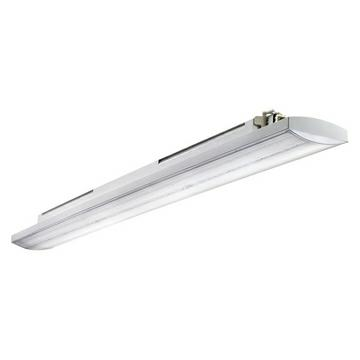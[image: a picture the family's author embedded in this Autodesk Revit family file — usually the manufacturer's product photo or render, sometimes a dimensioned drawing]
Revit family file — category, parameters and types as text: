
# Revit family: Lighting-Industriale-GEWISS-SMART[3]PLUS-PLAFONIERA-LED_TRANSPARENTE_FASCIOMEDIO_1600mm
name_source: partatom
category: Apparecchi per illuminazione
units: mm (PartAtom-declared; Revit-internal decimal feet)

## family parameters
Condiviso = No
Host = Superficie
Punto di calcolo locali = No
Quota connettore circolare = Usa diametro
Sorgente d'illuminazione = Sì
Taglio con vuoti quando caricato = No
Tipo di parte = Normale

## types (1)
- Lighting-Industriale-GEWISS-SMART[3]PLUS-PLAFONIERA-LED_TRANSPARENTE_FASCIOMEDIO_1600mm
    Angolo inclinazione = -90.00°
    Applicazione = Interno
    Carico apparente = 67 VA
    Catalogo = LIGHTING
    Catalogo Serie = SMART[3] PLUS
    Classe di efficienza LED integrati = A ÷ A++
    Classe isolamento = II
    Codice Electrocod = 2434
    Commenti sul wattaggio = 67W
    Descrizione = SMART3 PLUS 1600 T.W.DALI HE CONC 9 57
    Emetti da lunghezza linea = 1200 mm
    File diagramma fotometrico = GWS3323AC957.IES
    Filtro dei colori = 16777215
    Ganci = Alluminio
    Garanzia = 5 anni
    Glow Wire Test = 850°C
    Grado di protezione = IP66/IP69
    IDF = b404d7be-e00a-44e9-bc86-c84b1d72c067
    IDT = fe96ae85-68db-4e0d-8c9b-145f0d7eb605
    Immagine tipo = GWS3280TS.jpg
    Lampada = LED
    Lampada: = LED
    Lumen output (lm) = 5600
    Lunghezza = 1600 mm
    Lunghezza Lampada = 1600 mm  [stored 5.24934 ft]
    Modello = GWS3323AC957
    Numero poli = 2
    Potenza di sistema = 50 W
    Produttore = GEWISS S.p.A.
    Prospetto di default = 1219 mm
    Resistenza agli urti = IK08
    SEO = Plafoniera
    Scheda Tecnica = https://www.gewiss.com
    Schermo = Trasparente
    Schermo. = Led Acceso
    Stampa 1_100 = Sì
    Stampa 1_200 = No
    Struttura = GRIGIO
    Temperatura di colore = 5700 K (CRI > 90)
    Temperatura di colore: = 5700 K (CRI > 90)
    Temperatura di funzionamento = -25 +50 °C
    Temperatura di utilizzo = -25 +50 °C
    Tensione = 220-240 V
    Tipologia = DALI
    Tipologia sorgente luminosa = LED - Non sostituibile
    URL = https://www.gewiss.com
    Variazione temperatura colore lampada con luminosità attenuata = <Nessuno>
    Versione file RFA = 20.0

note: [stored X ft] marks values corroborated as IEEE doubles in the binary element streams (Revit-internal decimal feet)
